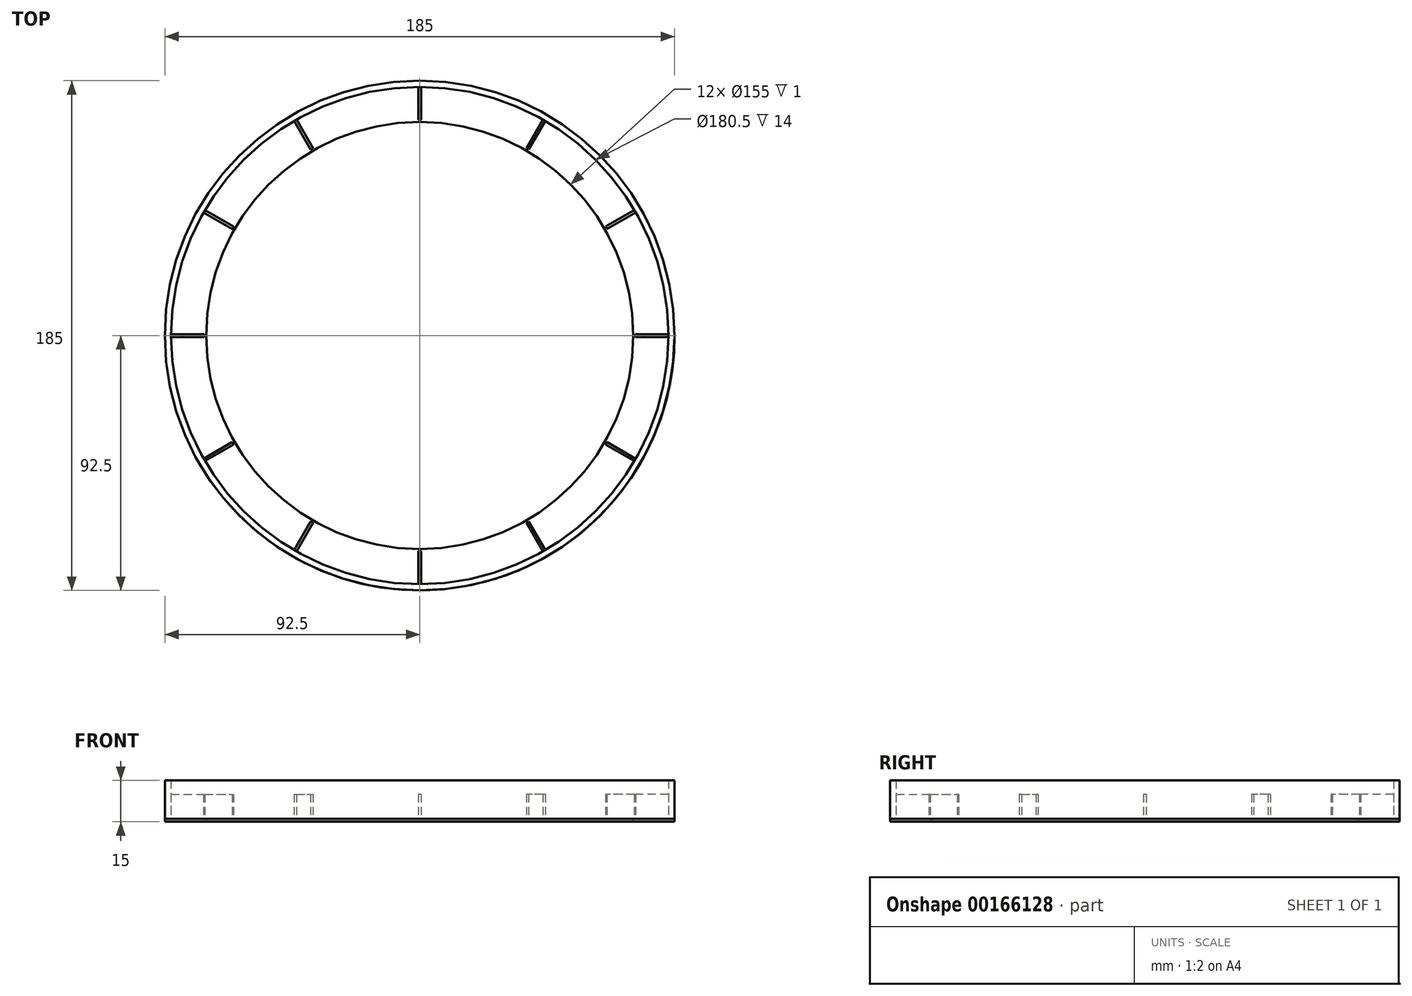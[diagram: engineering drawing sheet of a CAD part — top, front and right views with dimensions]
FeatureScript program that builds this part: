
annotation { "Feature Type Name" : "Feature", "Feature Type Description" : "" }
export const myFeature = defineFeature(function(context is Context, id is Id, definition is map)
    precondition{}
    {
        {
            var Q0;
            Q0=qCreatedBy(makeId("Top.planeOp"),FACE);
            var sketch = newSketch(context, id + "F0", { "sketchPlane" : qUnion([Q0])});
            skCircle(sketch, "E0", {"center": v(0, 0) * mm, "radius": 92.5 * mm});
            skCircle(sketch, "E1", {"center": v(0, 0) * mm, "radius": 77.5 * mm});
            skSolve(sketch);
        }
        {
            var Q0;
            Q0 = qSketchRegion(id + "F0", true);
            extrude(context, id + "F1", {"entities" : qUnion([Q0]), "depth" : 1 * mm});
        }
        {
            var Q0;
            Q0=makeQuery(id+"F1.opExtrude","CAP_FACE",FACE,{"disambiguationData":[OSD([sQuery(id+"F0.wireOp",EDGE,"E0"),sQuery(id+"F0.wireOp",EDGE,"E1")])],"isStart":false});
            var sketch = newSketch(context, id + "F2", { "sketchPlane" : qUnion([Q0])});
            skCircle(sketch, "E2", {"center": v(0, 0) * mm, "radius": 90.25 * mm});
            skCircle(sketch, "E3", {"center": v(0, 0) * mm, "radius": 78.25 * mm});
            skLineSegment(sketch, "E4", {"start": v(-90.25, 0.5) * mm, "end": v(-78.25, 0.5) * mm});
            skLineSegment(sketch, "E5", {"start": v(-90.25, -0.5) * mm, "end": v(-78.25, -0.5) * mm});
            skPoint(sketch, "E6.start.orphan", {"position": v(-78.25, 0) * mm});
            skCircle(sketch, "E7", {"center": v(0, 0) * mm, "radius": 92.5 * mm});
            skCircle(sketch, "E8", {"center": v(0, 0) * mm, "radius": 77.5 * mm});
            skSolve(sketch);
        }
        {
            var Q0;
            {var subQ0=sQuery(id+"F2.wireOp",EDGE,"E4");Q0=makeQuery(id+"F2.imprint","IMPRINT",FACE,{"disambiguationData":[TD([[makeQuery(id+"F2.imprint","IMPRINT",EDGE,{"derivedFrom":subQ0}),-1.0]])]});}
            extrude(context, id + "F3", {"entities" : qUnion([Q0]), "operationType" : NewBodyOperationType.ADD, "depth" : 9 * mm});
        }
        {
            var Q0;
            Q0=qCreatedBy(makeId("Right.planeOp"),FACE);
            var sketch = newSketch(context, id + "F4", { "sketchPlane" : qUnion([Q0])});
            skLineSegment(sketch, "E9", {"start": v(0, -33.38) * mm, "end": v(0, 32.24) * mm});
            skSolve(sketch);
        }
        {
            var Q0;
            Q0=makeQuery(id+"F1.opExtrude","SWEPT_BODY",BODY,{"disambiguationData":[OSD([sQuery(id+"F0.wireOp",EDGE,"E0"),sQuery(id+"F0.wireOp",EDGE,"E1")])]});
            var Q1;
            Q1=sQuery(id+"F4.wireOp",EDGE,"E9");
            circularPattern(context, id + "F5", {"entities" : qUnion([Q0]), "axis" : qUnion([Q1]), "angle" : 360 * degree, "instanceCount" : 12, "equalSpace" : true});
        }
        {
            var Q0;
            Q0 = qSketchRegion(id + "F2", true);
            extrude(context, id + "F6", {"entities" : qUnion([Q0]), "depth" : 14 * mm});
        }
        {
            var Q0;
            Q0=sQuery(id+"F2.wireOp",EDGE,"E3");
            var Q1;
            Q1=sQuery(id+"F2.wireOp",EDGE,"E8");
            extrude(context, id + "F7", {"bodyType" : ToolBodyType.SURFACE, "surfaceEntities" : qUnion([Q0, Q1]), "depth" : 10 * mm});
        }
    });
